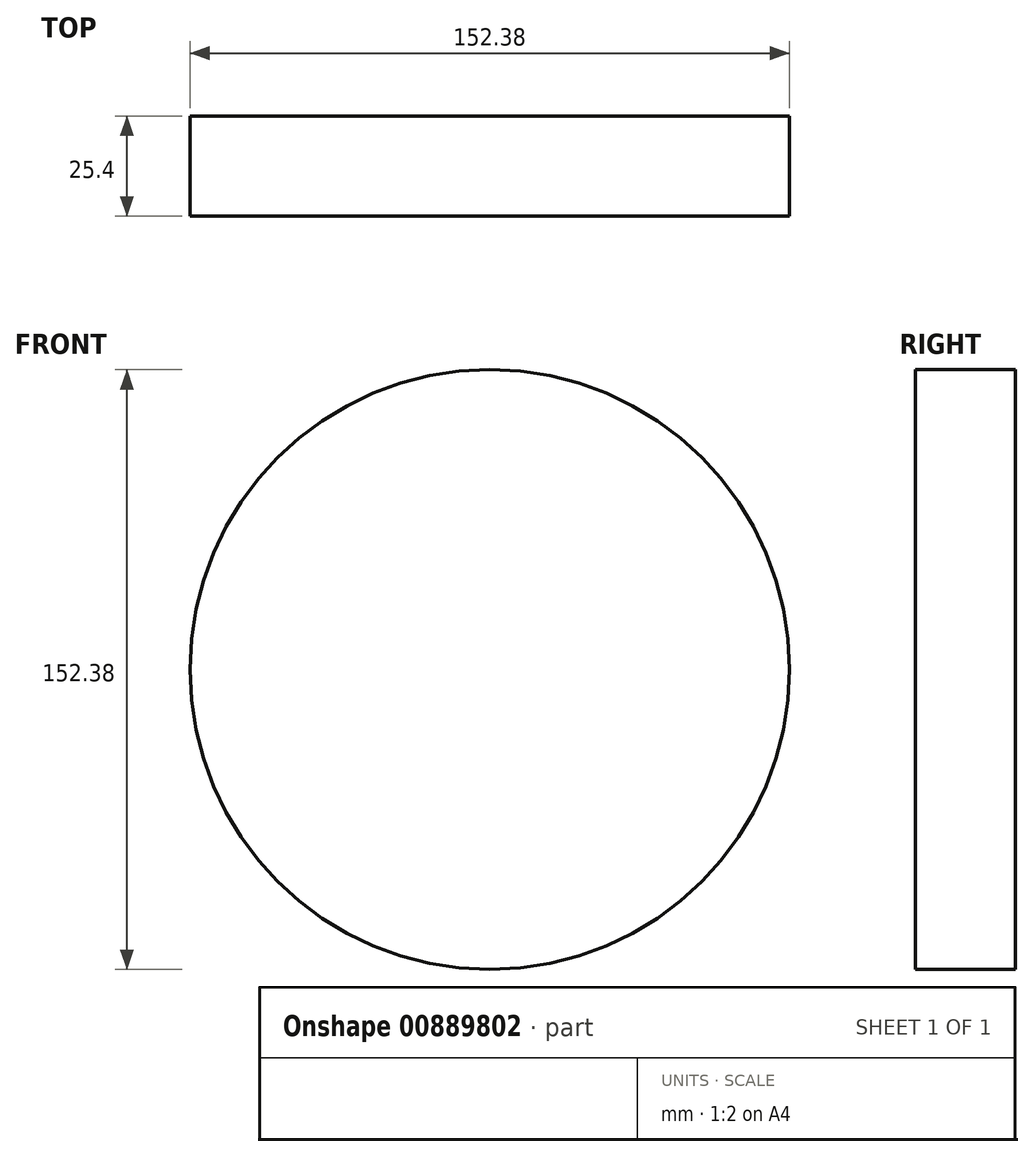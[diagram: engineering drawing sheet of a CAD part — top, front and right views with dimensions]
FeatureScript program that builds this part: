
annotation { "Feature Type Name" : "Feature", "Feature Type Description" : "" }
export const myFeature = defineFeature(function(context is Context, id is Id, definition is map)
    precondition{}
    {
        {
            var Q0;
            Q0=qCreatedBy(makeId("Front.planeOp"),FACE);
            var sketch = newSketch(context, id + "F0", { "sketchPlane" : qUnion([Q0])});
            skCircle(sketch, "E0", {"center": v(0, 0) * mm, "radius": 76.2 * mm});
            skSolve(sketch);
        }
        {
            var Q0;
            Q0=makeQuery(id+"F0.imprint","IMPRINT",FACE,{"disambiguationData":[TD([[makeQuery(id+"F0.imprint","IMPRINT",EDGE,{"derivedFrom":sQuery(id+"F0.wireOp",EDGE,"E0")}),1.0]])]});
            extrude(context, id + "F1", {"entities" : qUnion([Q0]), "depth" : 25.4 * mm, "offsetDistance" : 25.4 * mm});
        }
    });
